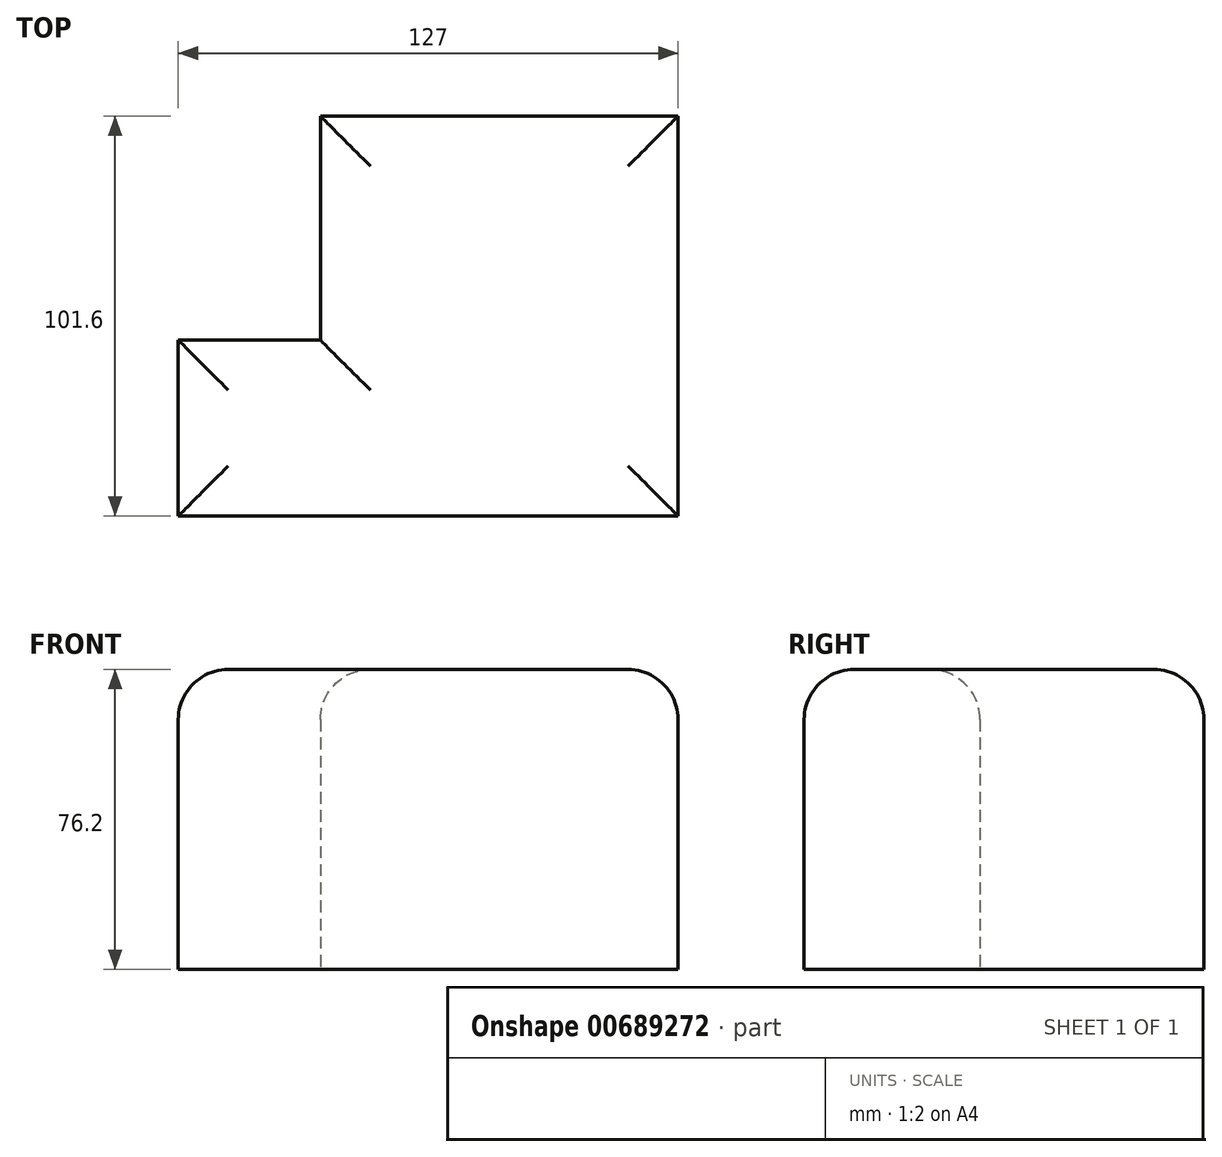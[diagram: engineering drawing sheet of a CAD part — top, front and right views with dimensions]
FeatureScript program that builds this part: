
annotation { "Feature Type Name" : "Feature", "Feature Type Description" : "" }
export const myFeature = defineFeature(function(context is Context, id is Id, definition is map)
    precondition{}
    {
        {
            var Q0;
            Q0=qCreatedBy(makeId("Top.planeOp"),FACE);
            var sketch = newSketch(context, id + "F0", { "sketchPlane" : qUnion([Q0])});
            skLineSegment(sketch, "E0.bottom", {"start": v(0, 0) * mm, "end": v(127, 0) * mm});
            skLineSegment(sketch, "E0.top", {"start": v(36.1, 101.6) * mm, "end": v(127, 101.6) * mm});
            skLineSegment(sketch, "E0.left", {"start": v(0, 0) * mm, "end": v(0, 44.7) * mm});
            skLineSegment(sketch, "E0.right", {"start": v(127, 0) * mm, "end": v(127, 101.6) * mm});
            skLineSegment(sketch, "E1", {"start": v(36.1, 101.6) * mm, "end": v(36.1, 44.7) * mm});
            skLineSegment(sketch, "E2", {"start": v(36.1, 44.7) * mm, "end": v(0, 44.7) * mm});
            skSolve(sketch);
        }
        {
            var Q0;
            Q0 = qSketchRegion(id + "F0", true);
            extrude(context, id + "F1", {"entities" : qUnion([Q0]), "depth" : 76.2 * mm, "offsetDistance" : 25.4 * mm});
        }
        {
            var Q0;
            Q0=makeQuery(id+"F1.opExtrude","CAP_EDGE",EDGE,{"disambiguationData":[OSD([sQuery(id+"F0.wireOp",EDGE,"E0.right")])],"isStart":false});
            var Q1;
            Q1=makeQuery(id+"F1.opExtrude","CAP_EDGE",EDGE,{"disambiguationData":[OSD([sQuery(id+"F0.wireOp",EDGE,"E0.top")])],"isStart":false});
            var Q2;
            Q2=makeQuery(id+"F1.opExtrude","CAP_EDGE",EDGE,{"disambiguationData":[OSD([sQuery(id+"F0.wireOp",EDGE,"E1")])],"isStart":false});
            var Q3;
            Q3=makeQuery(id+"F1.opExtrude","CAP_EDGE",EDGE,{"disambiguationData":[OSD([sQuery(id+"F0.wireOp",EDGE,"E2")])],"isStart":false});
            var Q4;
            Q4=makeQuery(id+"F1.opExtrude","CAP_EDGE",EDGE,{"disambiguationData":[OSD([sQuery(id+"F0.wireOp",EDGE,"E0.left")])],"isStart":false});
            var Q5;
            Q5=makeQuery(id+"F1.opExtrude","CAP_EDGE",EDGE,{"disambiguationData":[OSD([sQuery(id+"F0.wireOp",EDGE,"E0.bottom")])],"isStart":false});
            fillet(context, id + "F2", {"entities" : qUnion([Q0, Q1, Q2, Q3, Q4, Q5]), "radius" : 12.7 * mm, "tangentPropagation" : true, "allowEdgeOverflow" : false});
        }
    });
